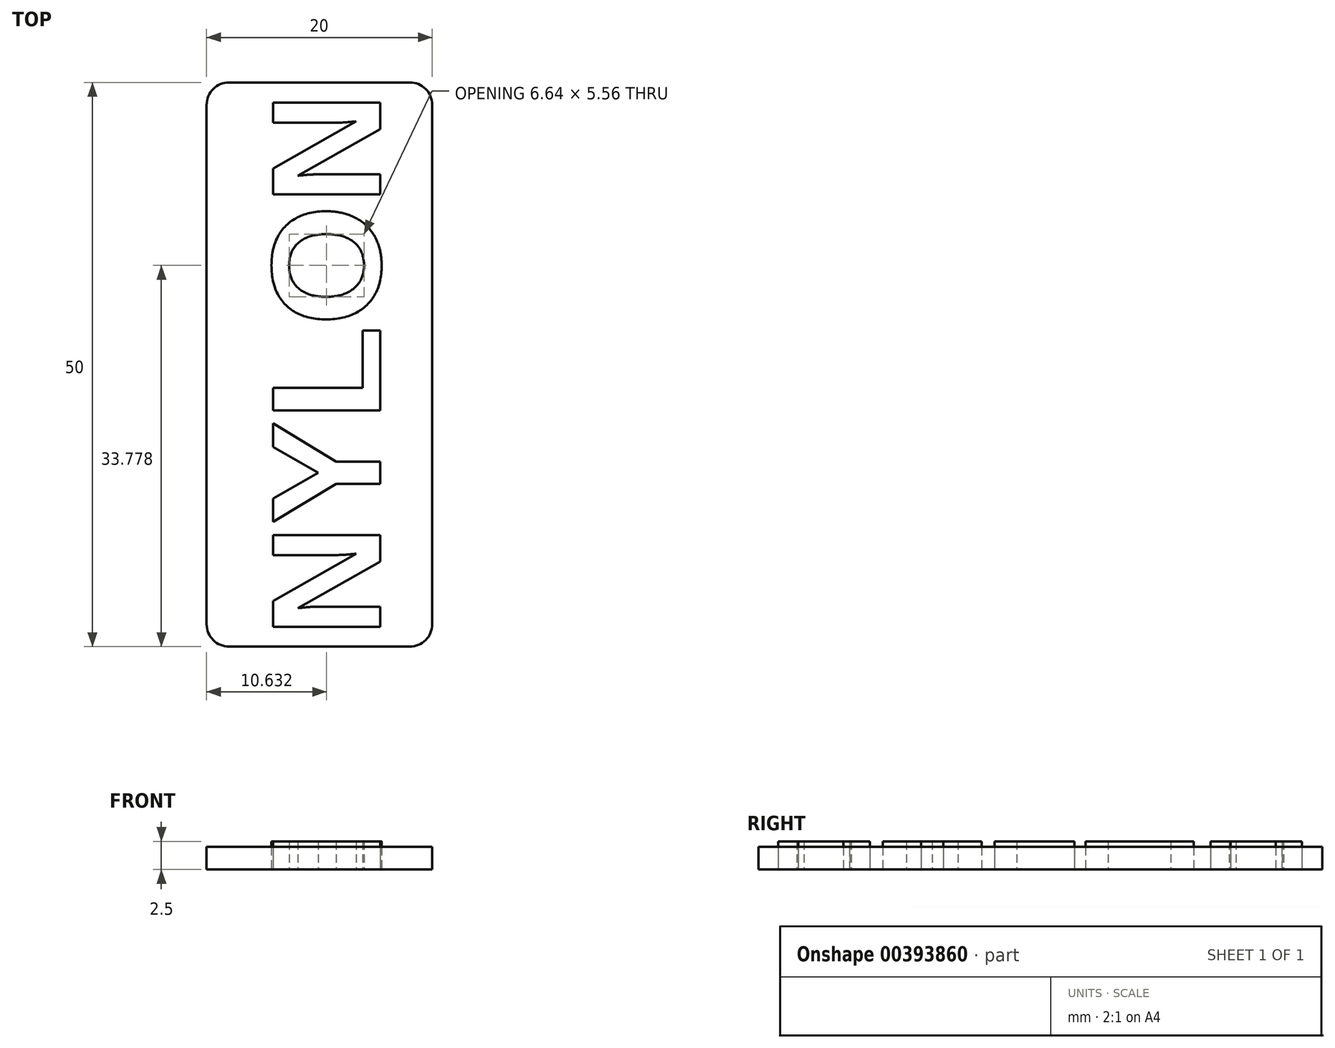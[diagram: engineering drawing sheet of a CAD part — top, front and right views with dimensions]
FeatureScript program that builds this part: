
annotation { "Feature Type Name" : "Feature", "Feature Type Description" : "" }
export const myFeature = defineFeature(function(context is Context, id is Id, definition is map)
    precondition{}
    {
        {
            var Q0;
            Q0=qCreatedBy(makeId("Top.planeOp"),FACE);
            var sketch = newSketch(context, id + "F0", { "sketchPlane" : qUnion([Q0])});
            skLineSegment(sketch, "E0.bottom", {"start": v(-20, -25) * mm, "end": v(0, -25) * mm});
            skLineSegment(sketch, "E0.top", {"start": v(-20, 25) * mm, "end": v(0, 25) * mm});
            skLineSegment(sketch, "E0.left", {"start": v(-20, -25) * mm, "end": v(-20, 25) * mm});
            skLineSegment(sketch, "E0.right", {"start": v(0, -25) * mm, "end": v(0, 25) * mm});
            skSolve(sketch);
        }
        {
            var Q0;
            Q0=makeQuery(id+"F0.imprint","IMPRINT",FACE,{"disambiguationData":[TD([[makeQuery(id+"F0.imprint","IMPRINT",EDGE,{"derivedFrom":sQuery(id+"F0.wireOp",EDGE,"E0.bottom")}),1.0]])]});
            extrude(context, id + "F1", {"entities" : qUnion([Q0]), "depth" : 2 * mm});
        }
        {
            var Q0;
            Q0=makeQuery(id+"F1.opExtrude","SWEPT_EDGE",EDGE,{"disambiguationData":[OSD([sQuery(id+"F0.wireOp",EDGE,"E0.bottom"),sQuery(id+"F0.wireOp",EDGE,"E0.right")])]});
            var Q1;
            Q1=makeQuery(id+"F1.opExtrude","SWEPT_EDGE",EDGE,{"disambiguationData":[OSD([sQuery(id+"F0.wireOp",EDGE,"E0.bottom"),sQuery(id+"F0.wireOp",EDGE,"E0.left")])]});
            var Q2;
            Q2=makeQuery(id+"F1.opExtrude","SWEPT_EDGE",EDGE,{"disambiguationData":[OSD([sQuery(id+"F0.wireOp",EDGE,"E0.top"),sQuery(id+"F0.wireOp",EDGE,"E0.right")])]});
            var Q3;
            Q3=makeQuery(id+"F1.opExtrude","SWEPT_EDGE",EDGE,{"disambiguationData":[OSD([sQuery(id+"F0.wireOp",EDGE,"E0.top"),sQuery(id+"F0.wireOp",EDGE,"E0.left")])]});
            fillet(context, id + "F2", {"entities" : qUnion([Q0, Q1, Q2, Q3]), "radius" : 2 * mm, "tangentPropagation" : true, "allowEdgeOverflow" : false});
        }
        {
            var Q0;
            Q0=qCreatedBy(makeId("Top.planeOp"),FACE);
            var sketch = newSketch(context, id + "F3", { "sketchPlane" : qUnion([Q0])});
            skText(sketch, "E1", { "text": "NYLON", "fontName": "Arimo-Bold.ttf"});
            const initialGuessF3  = {"E1": [-0.00462, -0.02415, 0, 1, 0.00993]};
            skSetInitialGuess(sketch, initialGuessF3);
            skSolve(sketch);
        }
        {
            var Q0;
            Q0=qSketchRegion(id+"F3",true);
            extrude(context, id + "F4", {"entities" : qUnion([Q0]), "depth" : 2.5 * mm});
        }
    });
